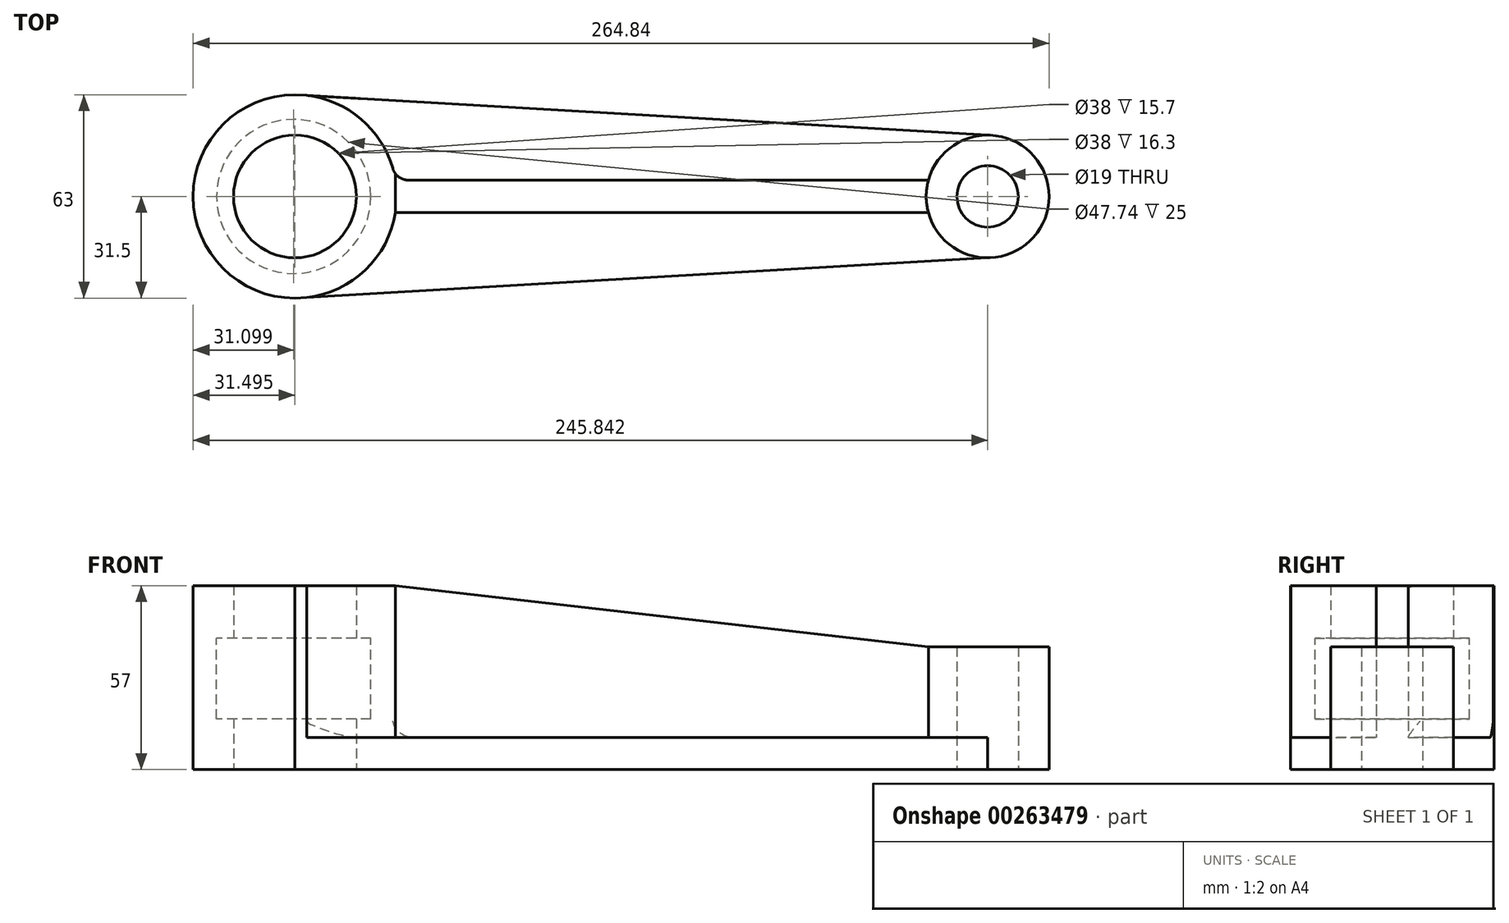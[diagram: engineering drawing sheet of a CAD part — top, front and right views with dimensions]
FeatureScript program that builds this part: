
annotation { "Feature Type Name" : "Feature", "Feature Type Description" : "" }
export const myFeature = defineFeature(function(context is Context, id is Id, definition is map)
    precondition{}
    {
        {
            var Q0;
            Q0=qCreatedBy(makeId("Top.planeOp"),FACE);
            var sketch = newSketch(context, id + "F0", { "sketchPlane" : qUnion([Q0])});
            skCircle(sketch, "E0", {"center": v(-147.41, 0) * mm, "radius": 19 * mm});
            skCircle(sketch, "E1", {"center": v(-147.41, 0) * mm, "radius": 31.5 * mm});
            skCircle(sketch, "E2", {"center": v(66.93, 0) * mm, "radius": 9.5 * mm});
            skCircle(sketch, "E3", {"center": v(66.93, 0) * mm, "radius": 19 * mm});
            skLineSegment(sketch, "E4", {"start": v(-147.42, 31.5) * mm, "end": v(66.93, 19) * mm});
            skLineSegment(sketch, "E5", {"start": v(-147.41, -31.5) * mm, "end": v(66.93, -19) * mm});
            skLineSegment(sketch, "E6", {"start": v(-116.32, 5.05) * mm, "end": v(48.62, 5.05) * mm});
            skLineSegment(sketch, "E7", {"start": v(48.59, -4.95) * mm, "end": v(-116.3, -4.95) * mm});
            skCircle(sketch, "E8", {"center": v(-147.41, 0) * mm, "radius": 24.74 * mm});
            skSolve(sketch);
        }
        {
            var Q0;
            {var subQ0=sQuery(id+"F0.wireOp",EDGE,"E7");Q0=makeQuery(id+"F0.imprint","IMPRINT",FACE,{"disambiguationData":[TD([[makeQuery(id+"F0.imprint","IMPRINT",EDGE,{"derivedFrom":subQ0}),1.0]])]});}
            var Q1;
            {var subQ0=sQuery(id+"F0.wireOp",EDGE,"E6");Q1=makeQuery(id+"F0.imprint","IMPRINT",FACE,{"disambiguationData":[TD([[makeQuery(id+"F0.imprint","IMPRINT",EDGE,{"derivedFrom":subQ0}),1.0]])]});}
            extrude(context, id + "F1", {"entities" : qUnion([Q0, Q1]), "depth" : 10 * mm});
        }
        {
            var Q0;
            {var subQ0=sQuery(id+"F0.wireOp",EDGE,"E6");Q0=makeQuery(id+"F0.imprint","IMPRINT",FACE,{"disambiguationData":[TD([[makeQuery(id+"F0.imprint","IMPRINT",EDGE,{"derivedFrom":subQ0}),-1.0]])]});}
            extrude(context, id + "F2", {"entities" : qUnion([Q0]), "depth" : 57 * mm});
        }
        {
            var Q0;
            Q0=makeQuery(id+"F0.imprint","IMPRINT",FACE,{"disambiguationData":[TD([[makeQuery(id+"F0.imprint","IMPRINT",EDGE,{"derivedFrom":sQuery(id+"F0.wireOp",EDGE,"E8")}),-1.0]])]});
            var Q1;
            Q1=makeQuery(id+"F0.imprint","IMPRINT",FACE,{"disambiguationData":[TD([[makeQuery(id+"F0.imprint","IMPRINT",EDGE,{"derivedFrom":sQuery(id+"F0.wireOp",EDGE,"E0")}),-1.0]])]});
            extrude(context, id + "F3", {"entities" : qUnion([Q0, Q1]), "operationType" : NewBodyOperationType.ADD, "depth" : 57 * mm});
        }
        {
            var Q0;
            Q0=makeQuery(id+"F0.imprint","IMPRINT",FACE,{"disambiguationData":[TD([[makeQuery(id+"F0.imprint","IMPRINT",EDGE,{"derivedFrom":sQuery(id+"F0.wireOp",EDGE,"E2")}),-1.0]])]});
            extrude(context, id + "F4", {"entities" : qUnion([Q0]), "operationType" : NewBodyOperationType.ADD, "depth" : 38 * mm});
        }
        {
            var Q0;
            Q0=makeQuery(id+"F2.opExtrude","SWEPT_FACE",FACE,{"disambiguationData":[OSD([sQuery(id+"F0.wireOp",EDGE,"E7")])]});
            var sketch = newSketch(context, id + "F5", { "sketchPlane" : qUnion([Q0])});
            skLineSegment(sketch, "E9", {"start": v(-116.3, 57) * mm, "end": v(48.59, 38) * mm});
            skLineSegment(sketch, "E10", {"start": v(48.59, 38) * mm, "end": v(48.59, 57) * mm});
            skLineSegment(sketch, "E11", {"start": v(48.59, 57) * mm, "end": v(-116.3, 57) * mm});
            skSolve(sketch);
        }
        {
            var Q0;
            Q0=makeQuery(id+"F5.imprint","IMPRINT",FACE,{"disambiguationData":[TD([[makeQuery(id+"F5.imprint","IMPRINT",EDGE,{"derivedFrom":sQuery(id+"F5.wireOp",EDGE,"E9")}),1.0]])]});
            extrude(context, id + "F6", {"entities" : qUnion([Q0]), "operationType" : NewBodyOperationType.REMOVE, "endBound" : BoundingType.SYMMETRIC, "oppositeDirection" : true, "depth" : 25 * mm});
        }
        {
            var Q0;
            Q0=makeQuery(id+"F1.opExtrude","CAP_EDGE",EDGE,{"disambiguationData":[OSD([sQuery(id+"F0.wireOp",EDGE,"E7")])],"isStart":false});
            var Q1;
            {var subQ0=sQuery(id+"F0.wireOp",EDGE,"E1");Q1=makeQuery(id+"F1.opExtrude","CAP_EDGE",EDGE,{"disambiguationData":[OSD([subQ0]),TDD([makeQuery(id+"F0.imprint","IMPRINT",EDGE,{"disambiguationData":[TD([[makeQuery(id+"F0.imprint","INTERSECT",VERTEX,{"derivedFrom":[subQ0,sQuery(id+"F0.wireOp",EDGE,"E7")]}),1.0]])],"derivedFrom":subQ0})])],"isStart":false});}
            var Q2;
            Q2=makeQuery(id+"F2.opExtrude","SWEPT_EDGE",EDGE,{"disambiguationData":[OSD([sQuery(id+"F0.wireOp",EDGE,"E1"),sQuery(id+"F0.wireOp",EDGE,"E7")])]});
            var Q3;
            {var subQ0=sQuery(id+"F0.wireOp",EDGE,"E7");var subQ1=sQuery(id+"F0.wireOp",EDGE,"E3");Q3=makeQuery(id+"F4.boolean.opBoolean","SPLIT",EDGE,{"disambiguationData":[topologyDisambiguationEdgeConnected([makeQuery(id+"F4.opExtrude","SWEPT_FACE",FACE,{"disambiguationData":[OSD([subQ1])]})])],"derivedFrom":makeQuery(id+"F2.opExtrude","SWEPT_EDGE",EDGE,{"disambiguationData":[OSD([subQ1,subQ0])]})});}
            var Q4;
            {var subQ0=sQuery(id+"F0.wireOp",EDGE,"E3");Q4=makeQuery(id+"F1.opExtrude","CAP_EDGE",EDGE,{"disambiguationData":[OSD([subQ0]),TDD([makeQuery(id+"F0.imprint","IMPRINT",EDGE,{"disambiguationData":[TD([[makeQuery(id+"F0.imprint","INTERSECT",VERTEX,{"derivedFrom":[subQ0,sQuery(id+"F0.wireOp",EDGE,"E5")]}),1.0]])],"derivedFrom":subQ0})])],"isStart":false});}
            var Q5;
            Q5=makeQuery(id+"F1.opExtrude","CAP_EDGE",EDGE,{"disambiguationData":[OSD([sQuery(id+"F0.wireOp",EDGE,"E6")])],"isStart":false});
            var Q6;
            {var subQ0=sQuery(id+"F0.wireOp",EDGE,"E6");var subQ1=sQuery(id+"F0.wireOp",EDGE,"E3");Q6=makeQuery(id+"F4.boolean.opBoolean","SPLIT",EDGE,{"disambiguationData":[topologyDisambiguationEdgeConnected([makeQuery(id+"F4.opExtrude","SWEPT_FACE",FACE,{"disambiguationData":[OSD([subQ1])]})])],"derivedFrom":makeQuery(id+"F2.opExtrude","SWEPT_EDGE",EDGE,{"disambiguationData":[OSD([subQ1,subQ0])]})});}
            var Q7;
            {var subQ0=sQuery(id+"F0.wireOp",EDGE,"E3");Q7=makeQuery(id+"F1.opExtrude","CAP_EDGE",EDGE,{"disambiguationData":[OSD([subQ0]),TDD([makeQuery(id+"F0.imprint","IMPRINT",EDGE,{"disambiguationData":[TD([[makeQuery(id+"F0.imprint","INTERSECT",VERTEX,{"derivedFrom":[subQ0,sQuery(id+"F0.wireOp",EDGE,"E4")]}),-1.0]])],"derivedFrom":subQ0})])],"isStart":false});}
            var Q8;
            {var subQ0=sQuery(id+"F0.wireOp",EDGE,"E1");Q8=makeQuery(id+"F1.opExtrude","CAP_EDGE",EDGE,{"disambiguationData":[OSD([subQ0]),TDD([makeQuery(id+"F0.imprint","IMPRINT",EDGE,{"disambiguationData":[TD([[makeQuery(id+"F0.imprint","INTERSECT",VERTEX,{"derivedFrom":[subQ0,sQuery(id+"F0.wireOp",EDGE,"E6")]}),-1.0]])],"derivedFrom":subQ0})])],"isStart":false});}
            var Q9;
            Q9=makeQuery(id+"F2.opExtrude","SWEPT_EDGE",EDGE,{"disambiguationData":[OSD([sQuery(id+"F0.wireOp",EDGE,"E1"),sQuery(id+"F0.wireOp",EDGE,"E6")])]});
            fillet(context, id + "F7", {"entities" : qUnion([Q0, Q1, Q2, Q3, Q4, Q5, Q6, Q7, Q8, Q9]), "radius" : 5 * mm, "tangentPropagation" : true, "allowEdgeOverflow" : false});
        }
        {
            var Q0;
            {var subQ0=sQuery(id+"F0.wireOp",EDGE,"E7");var subQ1=sQuery(id+"F0.wireOp",EDGE,"E5");var subQ2=sQuery(id+"F0.wireOp",EDGE,"E6");var subQ3=sQuery(id+"F0.wireOp",EDGE,"E4");var subQ4=sQuery(id+"F0.wireOp",EDGE,"E0");var subQ5=sQuery(id+"F0.wireOp",EDGE,"E1");Q0=makeQuery(id+"F6.boolean.opBoolean","SPLIT",FACE,{"disambiguationData":[TD([makeQuery(id+"F1.opExtrude","SWEPT_FACE",FACE,{"disambiguationData":[OSD([subQ3])]})])],"derivedFrom":makeQuery(id+"F3.boolean.opBoolean","MERGE",FACE,{"derivedFrom":[makeQuery(id+"F2.opExtrude","CAP_FACE",FACE,{"disambiguationData":[OSD([subQ5,sQuery(id+"F0.wireOp",EDGE,"E3"),subQ2,subQ0])],"isStart":false}),makeQuery(id+"F3.opExtrude","CAP_FACE",FACE,{"disambiguationData":[OSD([subQ4,subQ5,subQ3,subQ1])],"isStart":false})]})});}
            cPlane(context, id + "F8", {"entities" : qUnion([Q0]), "cplaneType" : CPlaneType.OFFSET, "offset" : 28.8 * mm, "oppositeDirection" : true, "width" : 150 * mm, "height" : 150 * mm});
        }
        {
            var Q0;
            Q0=qCreatedBy(id+"F8.planeOp",FACE);
            var sketch = newSketch(context, id + "F9", { "sketchPlane" : qUnion([Q0])});
            skCircle(sketch, "E12", {"center": v(-147.81, 0) * mm, "radius": 23.87 * mm});
            skSolve(sketch);
        }
        {
            var Q0;
            Q0=makeQuery(id+"F9.imprint","IMPRINT",FACE,{"disambiguationData":[TD([[makeQuery(id+"F9.imprint","IMPRINT",EDGE,{"derivedFrom":sQuery(id+"F9.wireOp",EDGE,"E12")}),1.0]])]});
            extrude(context, id + "F10", {"entities" : qUnion([Q0]), "operationType" : NewBodyOperationType.REMOVE, "endBound" : BoundingType.SYMMETRIC, "oppositeDirection" : true, "depth" : 25 * mm});
        }
    });
